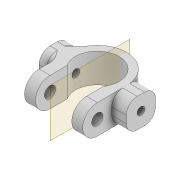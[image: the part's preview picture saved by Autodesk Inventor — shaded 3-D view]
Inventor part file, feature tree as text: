
AUTODESK INVENTOR PART (.ipt)
format: ipt  version: 2022 (Build 260153000, 153)  size: 245,760 bytes
history: native  units: mm
features: extrude x4, fillet x3, sketch x3, projected_geometry x2, mirror x1
ambient origin geometry x8: Origin, YZ Plane, XZ Plane, XY Plane, X Axis, Y Axis, Z Axis, Center Point
bodies: Solid1 (feature_tree)
feature tree (13):
  extrude  "Extrusion1"  Depth=2.0mm
  extrude  "Extrusion5"  Depth=8.0mm TaperAngle=0.0deg
  extrude  "Extrusion6"  Depth=3.0mm
  extrude  "Extrusion7"  Depth=2.0mm
  fillet  "Fillet4"  Radius=4.0mm
  fillet  "Fillet5"  Radius=100.0mm
  fillet  "Fillet6"  Radius=4.0mm
  mirror  "Mirror2"
  sketch  "Sketch6"  dims[d0=12.0mm d1=2.0mm]
  sketch  "Sketch7"  dims[d3=4.0mm d6=8.0mm d7=0.0mm]
  projected_geometry  "Projected Loop4"
  sketch  "Sketch8"  dims[d24=3.0mm d27=3.0mm d28=3.1mm d29=4.0mm d30=100.0mm d31=0.0mm d32=4.0mm d33=4.0mm d34=4.0mm d35=8.0mm d36=0.0mm d37=2.1mm d38=8.0mm d39=0.0mm d40=3.0mm d41=4.0mm d42=2.0mm]
  projected_geometry  "Projected Loop5"
